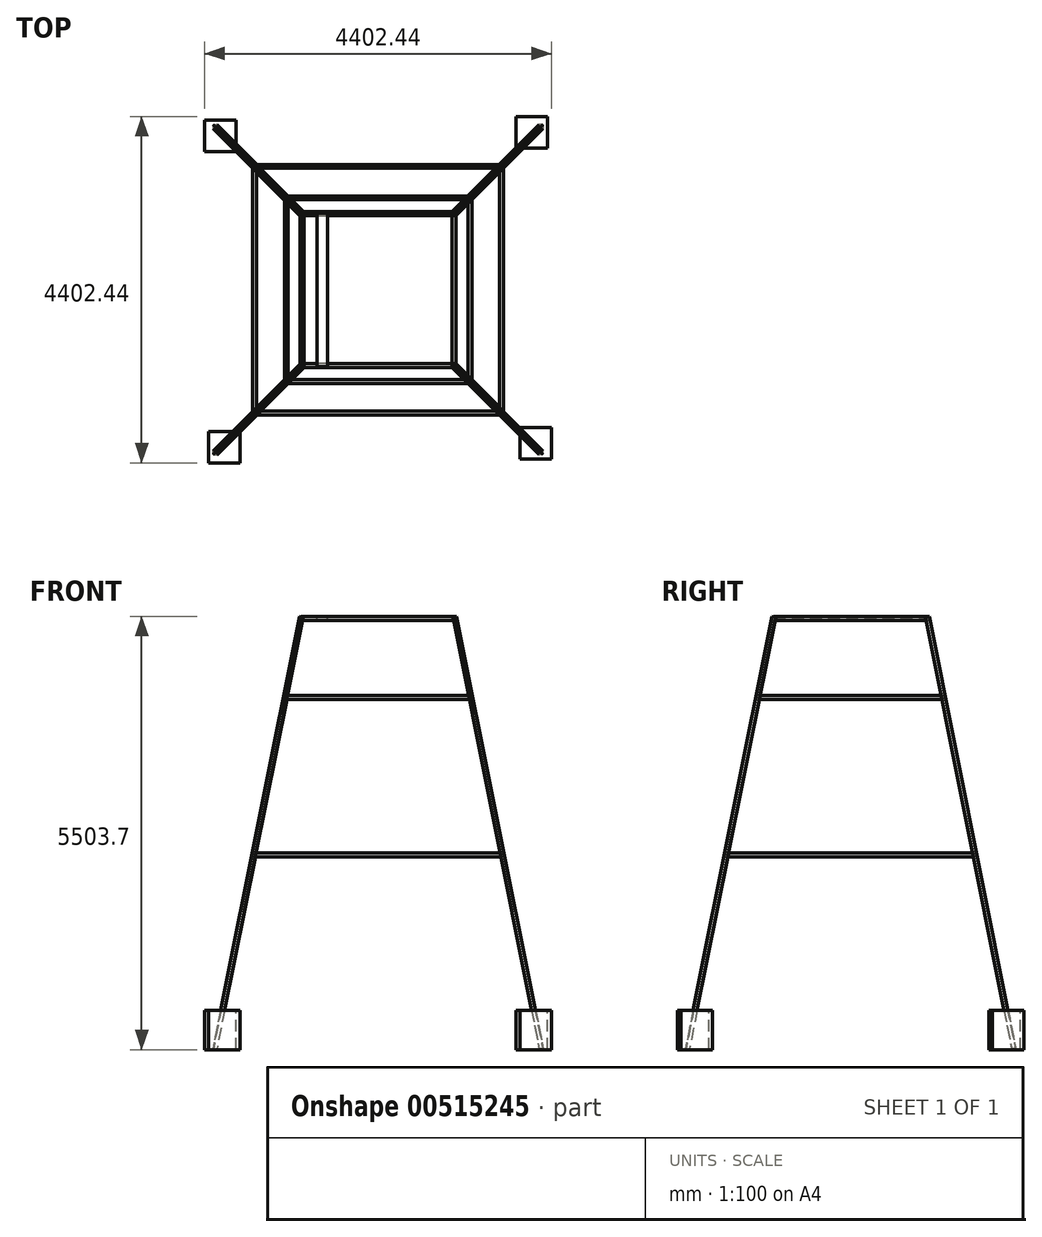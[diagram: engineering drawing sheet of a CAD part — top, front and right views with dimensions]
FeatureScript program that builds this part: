
annotation { "Feature Type Name" : "Feature", "Feature Type Description" : "" }
export const myFeature = defineFeature(function(context is Context, id is Id, definition is map)
    precondition{}
    {
        {
            var Q0;
            Q0=qCreatedBy(makeId("Top.planeOp"),FACE);
            cPlane(context, id + "F0", {"entities" : qUnion([Q0]), "cplaneType" : CPlaneType.OFFSET, "offset" : 5000 * mm, "width" : 150 * mm, "height" : 150 * mm});
        }
        {
            var Q0;
            Q0=qCreatedBy(makeId("Top.planeOp"),FACE);
            cPlane(context, id + "F1", {"entities" : qUnion([Q0]), "cplaneType" : CPlaneType.OFFSET, "offset" : 2000 * mm, "width" : 150 * mm, "height" : 150 * mm});
        }
        {
            var Q0;
            Q0=qCreatedBy(makeId("Top.planeOp"),FACE);
            cPlane(context, id + "F2", {"entities" : qUnion([Q0]), "cplaneType" : CPlaneType.OFFSET, "offset" : 4000 * mm, "width" : 150 * mm, "height" : 150 * mm});
        }
        {
            var Q0;
            Q0=qCreatedBy(makeId("Top.planeOp"),FACE);
            var sketch = newSketch(context, id + "F3", { "sketchPlane" : qUnion([Q0])});
            skLineSegment(sketch, "E0.bottom", {"start": v(2000, -2000) * mm, "end": v(-2000, -2000) * mm});
            skLineSegment(sketch, "E0.top", {"start": v(2000, 2000) * mm, "end": v(-2000, 2000) * mm});
            skLineSegment(sketch, "E0.left", {"start": v(2000, -2000) * mm, "end": v(2000, 2000) * mm});
            skLineSegment(sketch, "E0.right", {"start": v(-2000, -2000) * mm, "end": v(-2000, 2000) * mm});
            skPoint(sketch, "E0.middle", {"position": v(0, 0) * mm});
            skSolve(sketch);
        }
        {
            var Q0;
            Q0=qCreatedBy(id+"F0.planeOp",FACE);
            var sketch = newSketch(context, id + "F4", { "sketchPlane" : qUnion([Q0])});
            skLineSegment(sketch, "E1.bottom", {"start": v(1000, -1000) * mm, "end": v(-1000, -1000) * mm});
            skLineSegment(sketch, "E1.top", {"start": v(1000, 1000) * mm, "end": v(-1000, 1000) * mm});
            skLineSegment(sketch, "E1.left", {"start": v(1000, -1000) * mm, "end": v(1000, 1000) * mm});
            skLineSegment(sketch, "E1.right", {"start": v(-1000, -1000) * mm, "end": v(-1000, 1000) * mm});
            skPoint(sketch, "E1.middle", {"position": v(0, 0) * mm});
            skSolve(sketch);
        }
        {
            var Q0;
            Q0=sQuery(id+"F4.wireOp",VERTEX,"E1.right.start");
            var Q1;
            Q1=sQuery(id+"F3.wireOp",VERTEX,"E0.right.start");
            var Q2;
            Q2=sQuery(id+"F3.wireOp",VERTEX,"E0.middle");
            cPlane(context, id + "F5", {"entities" : qUnion([Q0, Q1, Q2]), "cplaneType" : CPlaneType.THREE_POINT, "offset" : 25 * mm, "width" : 150 * mm, "height" : 150 * mm});
        }
        {
            var Q0;
            Q0=qCreatedBy(id+"F5.planeOp",FACE);
            var sketch = newSketch(context, id + "F6", { "sketchPlane" : qUnion([Q0])});
            skPoint(sketch, "E2.0", {"position": v(1414.21, 5000) * mm});
            skPoint(sketch, "E3.0", {"position": v(2828.43, 0) * mm});
            skLineSegment(sketch, "E4", {"start": v(1414.21, 5000) * mm, "end": v(2828.43, 0) * mm});
            skSolve(sketch);
        }
        {
            var Q0;
            Q0=sQuery(id+"F6.wireOp",VERTEX,"E3.0");
            var Q1;
            Q1=sQuery(id+"F6.wireOp",EDGE,"E4");
            cPlane(context, id + "F7", {"entities" : qUnion([Q0, Q1]), "cplaneType" : CPlaneType.LINE_POINT, "offset" : 25 * mm, "width" : 150 * mm, "height" : 150 * mm});
        }
        {
            var Q0;
            Q0=qCreatedBy(id+"F7.planeOp",FACE);
            var sketch = newSketch(context, id + "F8", { "sketchPlane" : qUnion([Q0])});
            skPoint(sketch, "E5.0", {"position": v(-1887.13, 1961.16) * mm});
            skLineSegment(sketch, "E6", {"start": v(-1887.13, 1961.16) * mm, "end": v(-1887.13, 1911.16) * mm});
            skLineSegment(sketch, "E7", {"start": v(-1887.13, 1961.16) * mm, "end": v(-1837.13, 1961.16) * mm});
            skLineSegment(sketch, "E8.0", {"start": v(-1883.48, 1952.51) * mm, "end": v(-1883.48, 1914.81) * mm});
            skLineSegment(sketch, "E8.1", {"start": v(-1878.48, 1957.51) * mm, "end": v(-1840.78, 1957.51) * mm});
            skPoint(sketch, "E9.visualSharp", {"position": v(-1883.48, 1957.51) * mm});
            skArc(sketch, "E9.filletArc", {"start": v(-1878.48, 1957.51) * mm, "mid": v(-1882.01, 1956.05) * mm, "end": v(-1883.48, 1952.51) * mm});
            skArc(sketch, "E10", {"start": v(-1840.78, 1957.51) * mm, "mid": v(-1838.2, 1958.58) * mm, "end": v(-1837.13, 1961.16) * mm});
            skArc(sketch, "E11", {"start": v(-1883.48, 1914.81) * mm, "mid": v(-1884.55, 1912.23) * mm, "end": v(-1887.13, 1911.16) * mm});
            skPoint(sketch, "E12.orphan", {"position": v(-1849.03, 1961.16) * mm});
            skSolve(sketch);
        }
        {
            var Q0;
            Q0 = qSketchRegion(id + "F8", true);
            extrude(context, id + "F9", {"entities" : qUnion([Q0]), "oppositeDirection" : true, "depth" : 5200 * mm, "offsetDistance" : 25 * mm, "hasSecondDirection" : true, "secondDirectionOppositeDirection" : false, "secondDirectionDepth" : 500 * mm});
        }
        {
            var Q0;
            Q0=qCreatedBy(makeId("Front.planeOp"),FACE);
            var sketch = newSketch(context, id + "F10", { "sketchPlane" : qUnion([Q0])});
            skLineSegment(sketch, "E13", {"start": v(-1591.04, 2000) * mm, "end": v(-1591.04, 1950) * mm});
            skLineSegment(sketch, "E14", {"start": v(-1591.04, 1950) * mm, "end": v(-1587.54, 1950) * mm});
            skLineSegment(sketch, "E15", {"start": v(-1587.54, 1950) * mm, "end": v(-1587.54, 1996.5) * mm});
            skLineSegment(sketch, "E16", {"start": v(-1587.54, 1996.5) * mm, "end": v(-1541.04, 1996.5) * mm});
            skLineSegment(sketch, "E17", {"start": v(-1541.04, 1996.5) * mm, "end": v(-1541.04, 2000) * mm});
            skLineSegment(sketch, "E18", {"start": v(-1541.04, 2000) * mm, "end": v(-1591.04, 2000) * mm});
            skLineSegment(sketch, "E19.0", {"start": v(-1000, 5000) * mm, "end": v(-2000, 0) * mm, "construction": true});
            skLineSegment(sketch, "E20.0", {"start": v(-990.77, 5001.35) * mm, "end": v(-2087.74, -483.47) * mm, "construction": true});
            skLineSegment(sketch, "E21", {"start": v(-1191.04, 4000) * mm, "end": v(-1191.04, 3950) * mm});
            skLineSegment(sketch, "E22", {"start": v(-1191.04, 3950) * mm, "end": v(-1187.54, 3950) * mm});
            skLineSegment(sketch, "E23", {"start": v(-1187.54, 3950) * mm, "end": v(-1187.54, 3996.5) * mm});
            skLineSegment(sketch, "E24", {"start": v(-1187.54, 3996.5) * mm, "end": v(-1141.04, 3996.5) * mm});
            skLineSegment(sketch, "E25", {"start": v(-1141.04, 3996.5) * mm, "end": v(-1141.04, 4000) * mm});
            skLineSegment(sketch, "E26", {"start": v(-1141.04, 4000) * mm, "end": v(-1191.04, 4000) * mm});
            skLineSegment(sketch, "E27", {"start": v(-991.04, 4950) * mm, "end": v(-941.04, 4950) * mm});
            skLineSegment(sketch, "E28", {"start": v(-941.04, 4950) * mm, "end": v(-941.04, 4953.5) * mm});
            skLineSegment(sketch, "E29", {"start": v(-941.04, 4953.5) * mm, "end": v(-987.54, 4953.5) * mm});
            skLineSegment(sketch, "E30", {"start": v(-987.54, 4953.5) * mm, "end": v(-987.54, 5000) * mm});
            skLineSegment(sketch, "E31", {"start": v(-987.54, 5000) * mm, "end": v(-991.04, 5000) * mm});
            skLineSegment(sketch, "E32", {"start": v(-991.04, 5000) * mm, "end": v(-991.04, 4950) * mm});
            skLineSegment(sketch, "E33", {"start": v(0, 1384.65) * mm, "end": v(0, 3182.54) * mm, "construction": true});
            skSolve(sketch);
        }
        {
            var Q0;
            Q0=makeQuery(id+"F10.imprint","IMPRINT",FACE,{"disambiguationData":[TD([[makeQuery(id+"F10.imprint","IMPRINT",EDGE,{"derivedFrom":sQuery(id+"F10.wireOp",EDGE,"E13")}),1.0]])]});
            extrude(context, id + "F11", {"entities" : qUnion([Q0]), "endBound" : BoundingType.SYMMETRIC, "depth" : 3172 * mm, "offsetDistance" : 25 * mm});
        }
        {
            var Q0;
            Q0=makeQuery(id+"F10.imprint","IMPRINT",FACE,{"disambiguationData":[TD([[makeQuery(id+"F10.imprint","IMPRINT",EDGE,{"derivedFrom":sQuery(id+"F10.wireOp",EDGE,"E21")}),1.0]])]});
            extrude(context, id + "F12", {"entities" : qUnion([Q0]), "endBound" : BoundingType.SYMMETRIC, "depth" : 2366 * mm, "hasOffset" : true, "offsetDistance" : 25 * mm});
        }
        {
            var Q0;
            Q0=makeQuery(id+"F10.imprint","IMPRINT",FACE,{"disambiguationData":[TD([[makeQuery(id+"F10.imprint","IMPRINT",EDGE,{"derivedFrom":sQuery(id+"F10.wireOp",EDGE,"E27")}),1.0]])]});
            extrude(context, id + "F13", {"entities" : qUnion([Q0]), "endBound" : BoundingType.SYMMETRIC, "depth" : 1962 * mm, "offsetDistance" : 25 * mm});
        }
        {
            var Q0;
            Q0=makeQuery(id+"F11.opExtrude","SWEPT_FACE",FACE,{"disambiguationData":[OSD([sQuery(id+"F10.wireOp",EDGE,"E18")])]});
            var sketch = newSketch(context, id + "F14", { "sketchPlane" : qUnion([Q0])});
            skLineSegment(sketch, "E34", {"start": v(-1541.04, -1586) * mm, "end": v(-1586.04, -1586) * mm});
            skLineSegment(sketch, "E35", {"start": v(-1586.04, -1586) * mm, "end": v(-1541.04, -1541) * mm});
            skLineSegment(sketch, "E36", {"start": v(-1541.04, -1541) * mm, "end": v(-1541.04, -1586) * mm});
            skLineSegment(sketch, "E37.MirrorCS", {"start": v(-1541.04, 1586) * mm, "end": v(-1586.04, 1586) * mm});
            skLineSegment(sketch, "E38.MirrorCS", {"start": v(-1541.04, 1541) * mm, "end": v(-1541.04, 1586) * mm});
            skLineSegment(sketch, "E39.MirrorCS", {"start": v(-1586.04, 1586) * mm, "end": v(-1541.04, 1541) * mm});
            skSolve(sketch);
        }
        {
            var Q0;
            Q0=makeQuery(id+"F12.opExtrude","SWEPT_FACE",FACE,{"disambiguationData":[OSD([sQuery(id+"F10.wireOp",EDGE,"E26")])]});
            var sketch = newSketch(context, id + "F15", { "sketchPlane" : qUnion([Q0])});
            skLineSegment(sketch, "E40", {"start": v(-1141.04, -1183) * mm, "end": v(-1184.04, -1183) * mm});
            skLineSegment(sketch, "E41", {"start": v(-1184.04, -1183) * mm, "end": v(-1141.04, -1140) * mm});
            skLineSegment(sketch, "E42", {"start": v(-1141.04, -1140) * mm, "end": v(-1141.04, -1183) * mm});
            skLineSegment(sketch, "E43.MirrorCS", {"start": v(-1141.04, 1140) * mm, "end": v(-1141.04, 1183) * mm});
            skLineSegment(sketch, "E44.MirrorCS", {"start": v(-1141.04, 1183) * mm, "end": v(-1184.04, 1183) * mm});
            skLineSegment(sketch, "E45.MirrorCS", {"start": v(-1184.04, 1183) * mm, "end": v(-1141.04, 1140) * mm});
            skSolve(sketch);
        }
        {
            var Q0;
            Q0=makeQuery(id+"F13.opExtrude","SWEPT_FACE",FACE,{"disambiguationData":[OSD([sQuery(id+"F10.wireOp",EDGE,"E29")])]});
            var sketch = newSketch(context, id + "F16", { "sketchPlane" : qUnion([Q0])});
            skLineSegment(sketch, "E46", {"start": v(-941.04, -981) * mm, "end": v(-982.04, -981) * mm});
            skLineSegment(sketch, "E47", {"start": v(-982.04, -981) * mm, "end": v(-941.04, -940) * mm});
            skLineSegment(sketch, "E48", {"start": v(-941.04, -940) * mm, "end": v(-941.04, -981) * mm});
            skLineSegment(sketch, "E49.MirrorCS", {"start": v(-982.04, 981) * mm, "end": v(-941.04, 940) * mm});
            skLineSegment(sketch, "E50.MirrorCS", {"start": v(-941.04, 981) * mm, "end": v(-982.04, 981) * mm});
            skLineSegment(sketch, "E51.MirrorCS", {"start": v(-941.04, 940) * mm, "end": v(-941.04, 981) * mm});
            skSolve(sketch);
        }
        {
            var Q0;
            Q0=makeQuery(id+"F3.imprint","IMPRINT",FACE,{"disambiguationData":[TD([[makeQuery(id+"F3.imprint","IMPRINT",EDGE,{"derivedFrom":sQuery(id+"F3.wireOp",EDGE,"E0.bottom")}),-1.0]])]});
            var sketch = newSketch(context, id + "F17", { "sketchPlane" : qUnion([Q0])});
            skLineSegment(sketch, "E52.bottom", {"start": v(-2154.1, -1801.22) * mm, "end": v(-1754.1, -1801.22) * mm});
            skLineSegment(sketch, "E52.top", {"start": v(-2154.1, -2201.22) * mm, "end": v(-1754.1, -2201.22) * mm});
            skLineSegment(sketch, "E52.left", {"start": v(-2154.1, -1801.22) * mm, "end": v(-2154.1, -2201.22) * mm});
            skLineSegment(sketch, "E52.right", {"start": v(-1754.1, -1801.22) * mm, "end": v(-1754.1, -2201.22) * mm});
            skPoint(sketch, "E52.middle", {"position": v(-1954.1, -2001.22) * mm});
            skSolve(sketch);
        }
        {
            var Q0;
            {var subQ0=sQuery(id+"F17.wireOp",EDGE,"E52.right");var subQ1=sQuery(id+"F17.wireOp",EDGE,"E52.bottom");var subQ2=makeQuery(id+"F17.imprint","INTERSECT",VERTEX,{"derivedFrom":[subQ1,subQ0]});Q0=makeQuery(id+"F17.imprint","IMPRINT",FACE,{"disambiguationData":[TD([[makeQuery(id+"F17.imprint","IMPRINT",EDGE,{"disambiguationData":[TD([[subQ2,1.0]])],"derivedFrom":subQ1}),-1.0]])]});}
            var Q1;
            {var subQ1=sQuery(id+"F17.wireOp",EDGE,"E52.top");Q1=makeQuery(id+"F17.imprint","IMPRINT",FACE,{"disambiguationData":[TD([[makeQuery(id+"F17.imprint","IMPRINT",EDGE,{"derivedFrom":subQ1}),1.0]])]});}
            extrude(context, id + "F18", {"entities" : qUnion([Q0, Q1]), "oppositeDirection" : true, "depth" : 500 * mm, "offsetDistance" : 25 * mm});
        }
        {
            var Q0;
            Q0=makeQuery(id+"F18.opExtrude","SWEPT_BODY",BODY,{"disambiguationData":[OSD([sQuery(id+"F17.wireOp",EDGE,"E52.bottom"),sQuery(id+"F17.wireOp",EDGE,"E52.top"),sQuery(id+"F17.wireOp",EDGE,"E52.left"),sQuery(id+"F17.wireOp",EDGE,"E52.right")])]});
            var Q1;
            Q1=makeQuery(id+"F9.opExtrude","SWEPT_BODY",BODY,{"disambiguationData":[OSD([sQuery(id+"F8.wireOp",EDGE,"E6"),sQuery(id+"F8.wireOp",EDGE,"E7"),sQuery(id+"F8.wireOp",EDGE,"E8.0"),sQuery(id+"F8.wireOp",EDGE,"E8.1"),sQuery(id+"F8.wireOp",EDGE,"E9.filletArc"),sQuery(id+"F8.wireOp",EDGE,"E10"),sQuery(id+"F8.wireOp",EDGE,"E11")])]});
            var Q2;
            Q2=makeQuery(id+"F11.opExtrude","SWEPT_BODY",BODY,{"disambiguationData":[OSD([sQuery(id+"F10.wireOp",EDGE,"E13"),sQuery(id+"F10.wireOp",EDGE,"E14"),sQuery(id+"F10.wireOp",EDGE,"E15"),sQuery(id+"F10.wireOp",EDGE,"E16"),sQuery(id+"F10.wireOp",EDGE,"E17"),sQuery(id+"F10.wireOp",EDGE,"E18")])]});
            var Q3;
            Q3=makeQuery(id+"F12.opExtrude","SWEPT_BODY",BODY,{"disambiguationData":[OSD([sQuery(id+"F10.wireOp",EDGE,"E21"),sQuery(id+"F10.wireOp",EDGE,"E22"),sQuery(id+"F10.wireOp",EDGE,"E23"),sQuery(id+"F10.wireOp",EDGE,"E24"),sQuery(id+"F10.wireOp",EDGE,"E25"),sQuery(id+"F10.wireOp",EDGE,"E26")])]});
            var Q4;
            Q4=makeQuery(id+"F13.opExtrude","SWEPT_BODY",BODY,{"disambiguationData":[OSD([sQuery(id+"F10.wireOp",EDGE,"E27"),sQuery(id+"F10.wireOp",EDGE,"E28"),sQuery(id+"F10.wireOp",EDGE,"E29"),sQuery(id+"F10.wireOp",EDGE,"E30"),sQuery(id+"F10.wireOp",EDGE,"E31"),sQuery(id+"F10.wireOp",EDGE,"E32")])]});
            var Q5;
            Q5=sQuery(id+"F10.wireOp",EDGE,"E33");
            circularPattern(context, id + "F19", {"entities" : qUnion([Q0, Q1, Q2, Q3, Q4]), "axis" : qUnion([Q5]), "angle" : 360 * degree, "instanceCount" : 4, "equalSpace" : true});
        }
        {
            var Q0;
            Q0=qCreatedBy(makeId("Front.planeOp"),FACE);
            var sketch = newSketch(context, id + "F20", { "sketchPlane" : qUnion([Q0])});
            skLineSegment(sketch, "E53.bottom", {"start": v(-643.58, 4953.5) * mm, "end": v(-776.93, 4953.5) * mm});
            skLineSegment(sketch, "E53.top", {"start": v(-643.58, 4991.6) * mm, "end": v(-776.93, 4991.6) * mm});
            skLineSegment(sketch, "E53.left", {"start": v(-643.58, 4953.5) * mm, "end": v(-643.58, 4991.6) * mm});
            skLineSegment(sketch, "E53.right", {"start": v(-776.93, 4953.5) * mm, "end": v(-776.93, 4991.6) * mm});
            skSolve(sketch);
        }
        {
            var Q0;
            Q0 = qSketchRegion(id + "F20", true);
            extrude(context, id + "F21", {"entities" : qUnion([Q0]), "endBound" : BoundingType.SYMMETRIC, "depth" : 1950 * mm, "offsetDistance" : 25 * mm});
        }
    });
